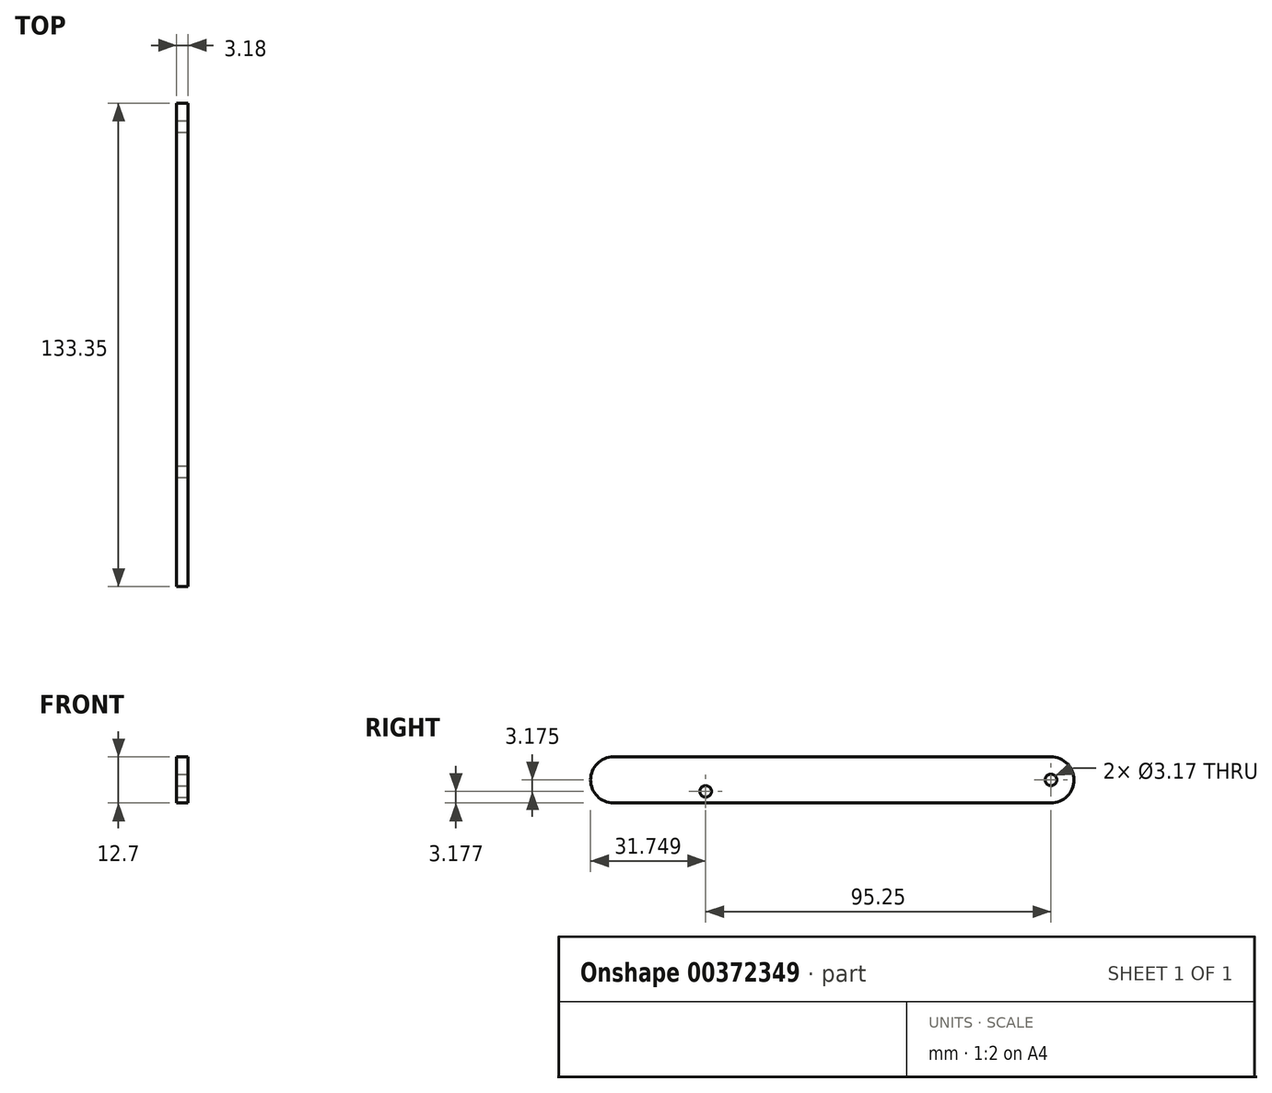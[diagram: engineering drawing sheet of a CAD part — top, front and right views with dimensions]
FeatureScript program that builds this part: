
annotation { "Feature Type Name" : "Feature", "Feature Type Description" : "" }
export const myFeature = defineFeature(function(context is Context, id is Id, definition is map)
    precondition{}
    {
        {
            var Q0;
            Q0=qCreatedBy(makeId("Right.planeOp"),FACE);
            var sketch = newSketch(context, id + "F0", { "sketchPlane" : qUnion([Q0])});
            skLineSegment(sketch, "E0.bottom", {"start": v(-41.93, 43.72) * mm, "end": v(78.72, 43.72) * mm});
            skLineSegment(sketch, "E0.top", {"start": v(-41.93, 31.02) * mm, "end": v(78.72, 31.02) * mm});
            skArc(sketch, "E1", {"start": v(-41.93, 43.72) * mm, "mid": v(-48.28, 37.37) * mm, "end": v(-41.93, 31.02) * mm});
            skArc(sketch, "E2", {"start": v(78.72, 31.02) * mm, "mid": v(85.07, 37.37) * mm, "end": v(78.72, 43.72) * mm});
            skPoint(sketch, "E3", {"position": v(-48.28, 37.37) * mm});
            skPoint(sketch, "E4", {"position": v(85.07, 37.37) * mm});
            skSolve(sketch);
        }
        {
            var Q0;
            Q0=qCreatedBy(makeId("Right.planeOp"),FACE);
            var sketch = newSketch(context, id + "F1", { "sketchPlane" : qUnion([Q0])});
            skCircle(sketch, "E5", {"center": v(-16.53, 34.2) * mm, "radius": 1.59 * mm});
            skSolve(sketch);
        }
        {
            var Q0;
            Q0=qCreatedBy(makeId("Right.planeOp"),FACE);
            var sketch = newSketch(context, id + "F2", { "sketchPlane" : qUnion([Q0])});
            skCircle(sketch, "E6", {"center": v(78.72, 37.37) * mm, "radius": 1.59 * mm});
            skSolve(sketch);
        }
        {
            var Q0;
            Q0 = qSketchRegion(id + "F0", true);
            extrude(context, id + "F3", {"entities" : qUnion([Q0]), "endBound" : BoundingType.SYMMETRIC, "depth" : 3.17 * mm});
        }
        {
            var Q0;
            Q0 = qSketchRegion(id + "F1", true);
            var Q1;
            Q1 = qSketchRegion(id + "F2", true);
            extrude(context, id + "F4", {"entities" : qUnion([Q0, Q1]), "operationType" : NewBodyOperationType.REMOVE, "endBound" : BoundingType.SYMMETRIC, "oppositeDirection" : true, "depth" : 25.4 * mm});
        }
    });
